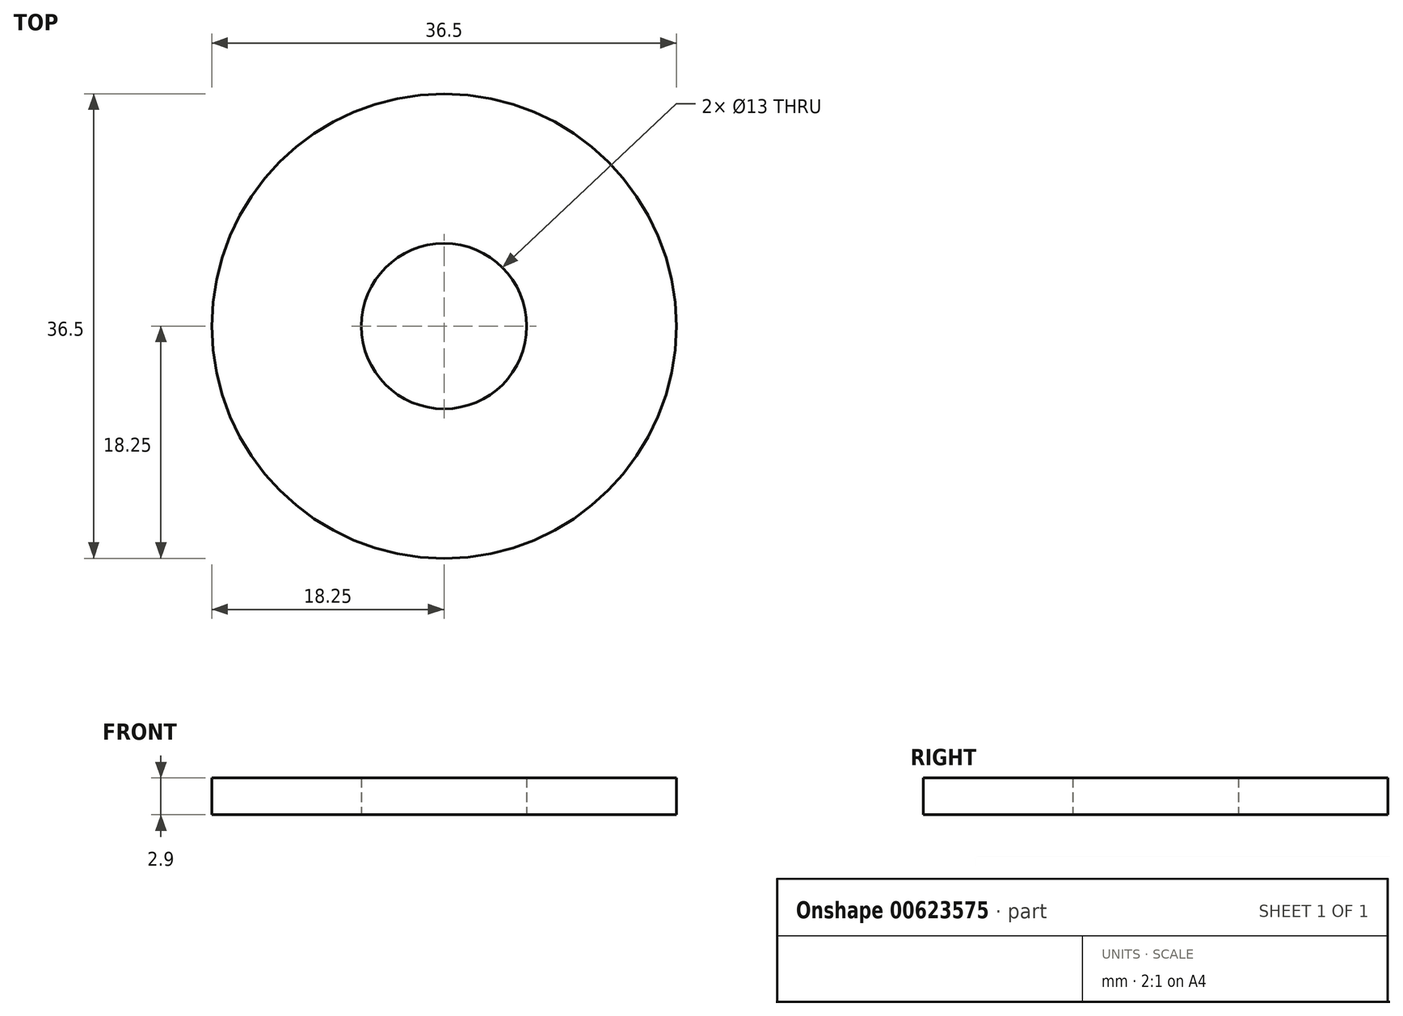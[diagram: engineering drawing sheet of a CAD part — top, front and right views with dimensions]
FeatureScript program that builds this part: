
annotation { "Feature Type Name" : "Feature", "Feature Type Description" : "" }
export const myFeature = defineFeature(function(context is Context, id is Id, definition is map)
    precondition{}
    {
        {
            var Q0;
            Q0=qCreatedBy(makeId("Top.planeOp"),FACE);
            var sketch = newSketch(context, id + "F0", { "sketchPlane" : qUnion([Q0])});
            skCircle(sketch, "E0", {"center": v(0, 0) * mm, "radius": 6.5 * mm});
            skCircle(sketch, "E1", {"center": v(0, 0) * mm, "radius": 18.25 * mm});
            skSolve(sketch);
        }
        {
            var Q0;
            Q0 = qSketchRegion(id + "F0", true);
            extrude(context, id + "F1", {"entities" : qUnion([Q0]), "depth" : 2.9 * mm, "offsetDistance" : 25 * mm});
        }
    });
